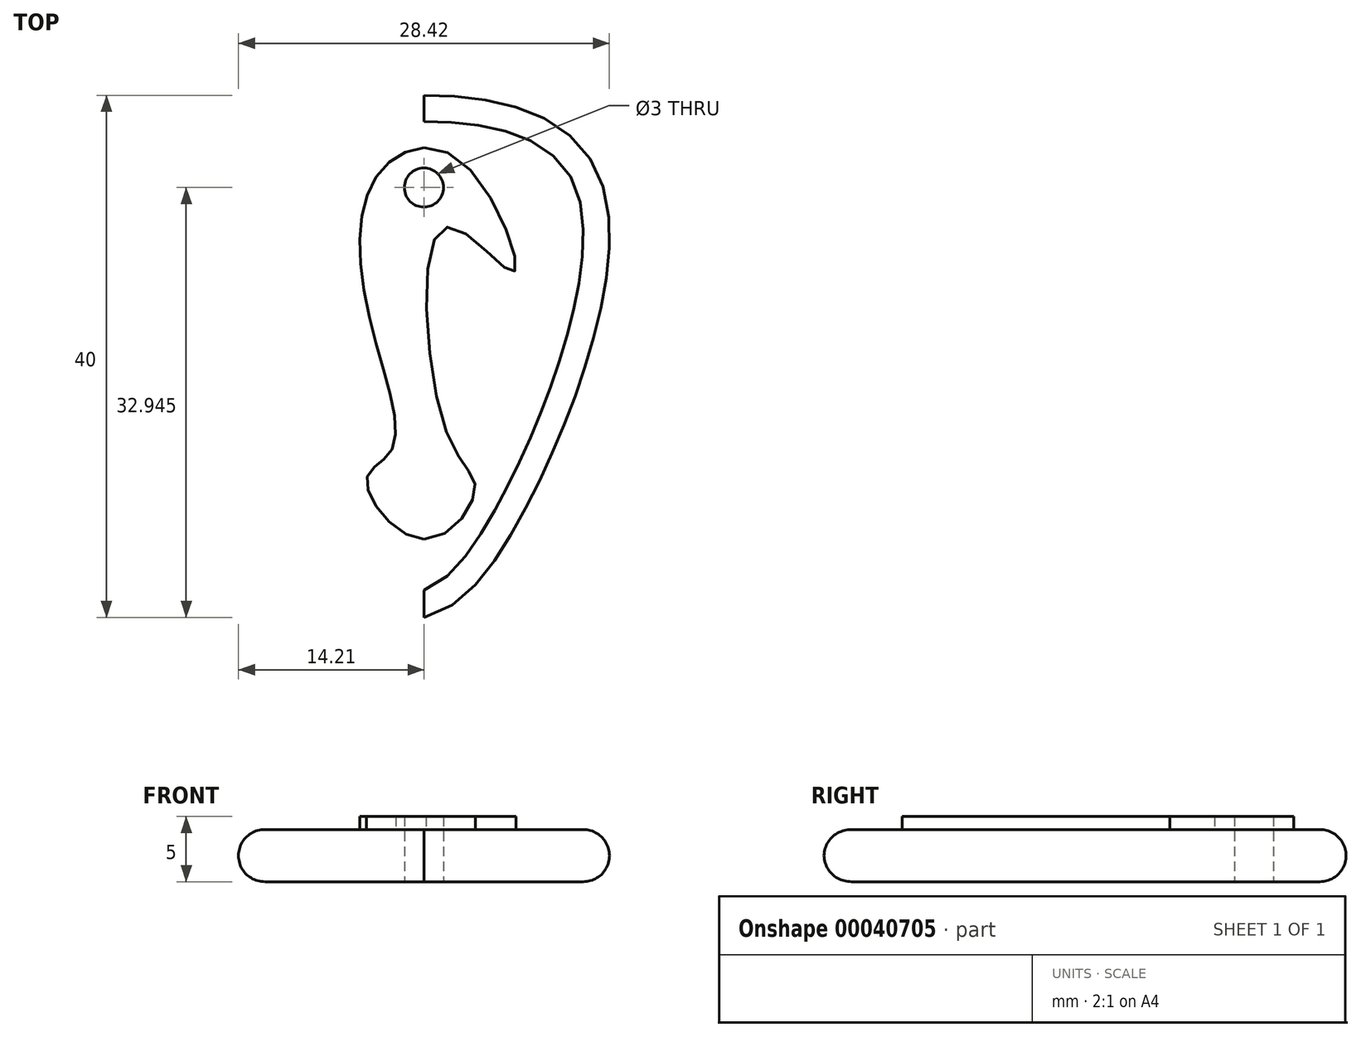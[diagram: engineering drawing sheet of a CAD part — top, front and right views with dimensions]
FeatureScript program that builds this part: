
annotation { "Feature Type Name" : "Feature", "Feature Type Description" : "" }
export const myFeature = defineFeature(function(context is Context, id is Id, definition is map)
    precondition{}
    {
        {
            var Q0;
            Q0=qCreatedBy(makeId("Top.planeOp"),FACE);
            var sketch = newSketch(context, id + "F0", { "sketchPlane" : qUnion([Q0])});
            skFitSpline(sketch, "E0", {"points": [v(0, 17.19) * mm, v(13.78, 10) * mm, v(6.54, -16.68) * mm, v(0, -22.81) * mm], "startDerivative": vector(62.6, 0.57) * mm, "endDerivative": vector(-30.24, -8.1) * mm});
            skLineSegment(sketch, "E1", {"start": v(0, 17.19) * mm, "end": v(0, -22.81) * mm});
            skFitSpline(sketch, "E2.MirrorCS", {"points": [v(0, 17.19) * mm, v(-13.78, 10) * mm, v(-6.54, -16.68) * mm, v(0, -22.81) * mm], "startDerivative": vector(-62.6, 0.57) * mm, "endDerivative": vector(30.24, -8.1) * mm});
            skSolve(sketch);
        }
        {
            var Q0;
            Q0 = qSketchRegion(id + "F0", true);
            extrude(context, id + "F1", {"entities" : qUnion([Q0]), "depth" : 4 * mm});
        }
        {
            var Q0;
            Q0=makeQuery(id+"F1.opExtrude","CAP_FACE",FACE,{"disambiguationData":[OSD([sQuery(id+"F0.wireOp",EDGE,"E0"),sQuery(id+"F0.wireOp",EDGE,"E2.MirrorCS")])],"isStart":false});
            var Q1;
            Q1=makeQuery(id+"F1.opExtrude","CAP_FACE",FACE,{"disambiguationData":[OSD([sQuery(id+"F0.wireOp",EDGE,"E0"),sQuery(id+"F0.wireOp",EDGE,"E2.MirrorCS")])],"isStart":true});
            fillet(context, id + "F2", {"entities" : qUnion([Q0, Q1]), "radius" : 2 * mm, "tangentPropagation" : true, "allowEdgeOverflow" : false});
        }
        {
            var Q0;
            Q0=makeQuery(id+"F1.opExtrude","CAP_FACE",FACE,{"disambiguationData":[OSD([sQuery(id+"F0.wireOp",EDGE,"E0"),sQuery(id+"F0.wireOp",EDGE,"E2.MirrorCS")])],"isStart":false});
            var sketch = newSketch(context, id + "F3", { "sketchPlane" : qUnion([Q0])});
            skFitSpline(sketch, "E3", {"points": [v(-2.46, -9.96) * mm, v(-4.4, -12.28) * mm, v(0, -16.82) * mm, v(3.91, -13.07) * mm, v(1.86, -8.94) * mm, v(1.74, 7.09) * mm, v(6.85, 3.68) * mm, v(2.7, 12.28) * mm, v(-3.57, 11.06) * mm, v(-4.14, 0) * mm, v(-2.46, -9.96) * mm]});
            skLineSegment(sketch, "E4", {"start": v(0, 13.18) * mm, "end": v(0, -16.82) * mm});
            skSolve(sketch);
        }
        {
            var Q0;
            Q0 = qSketchRegion(id + "F3", true);
            extrude(context, id + "F4", {"entities" : qUnion([Q0]), "operationType" : NewBodyOperationType.ADD, "depth" : 1 * mm});
        }
        {
            var Q0;
            Q0=makeQuery(id+"F1.opExtrude","CAP_FACE",FACE,{"disambiguationData":[OSD([sQuery(id+"F0.wireOp",EDGE,"E0"),sQuery(id+"F0.wireOp",EDGE,"E2.MirrorCS")])],"isStart":true});
            var sketch = newSketch(context, id + "F5", { "sketchPlane" : qUnion([Q0])});
            skCircle(sketch, "E5", {"center": v(0, -10.13) * mm, "radius": 1.5 * mm});
            skSolve(sketch);
        }
        {
            var Q0;
            Q0=makeQuery(id+"F5.imprint","IMPRINT",FACE,{"disambiguationData":[TD([[makeQuery(id+"F5.imprint","IMPRINT",EDGE,{"derivedFrom":sQuery(id+"F5.wireOp",EDGE,"E5")}),1.0]])]});
            extrude(context, id + "F6", {"entities" : qUnion([Q0]), "operationType" : NewBodyOperationType.REMOVE, "oppositeDirection" : true, "depth" : 25 * mm});
        }
    });
